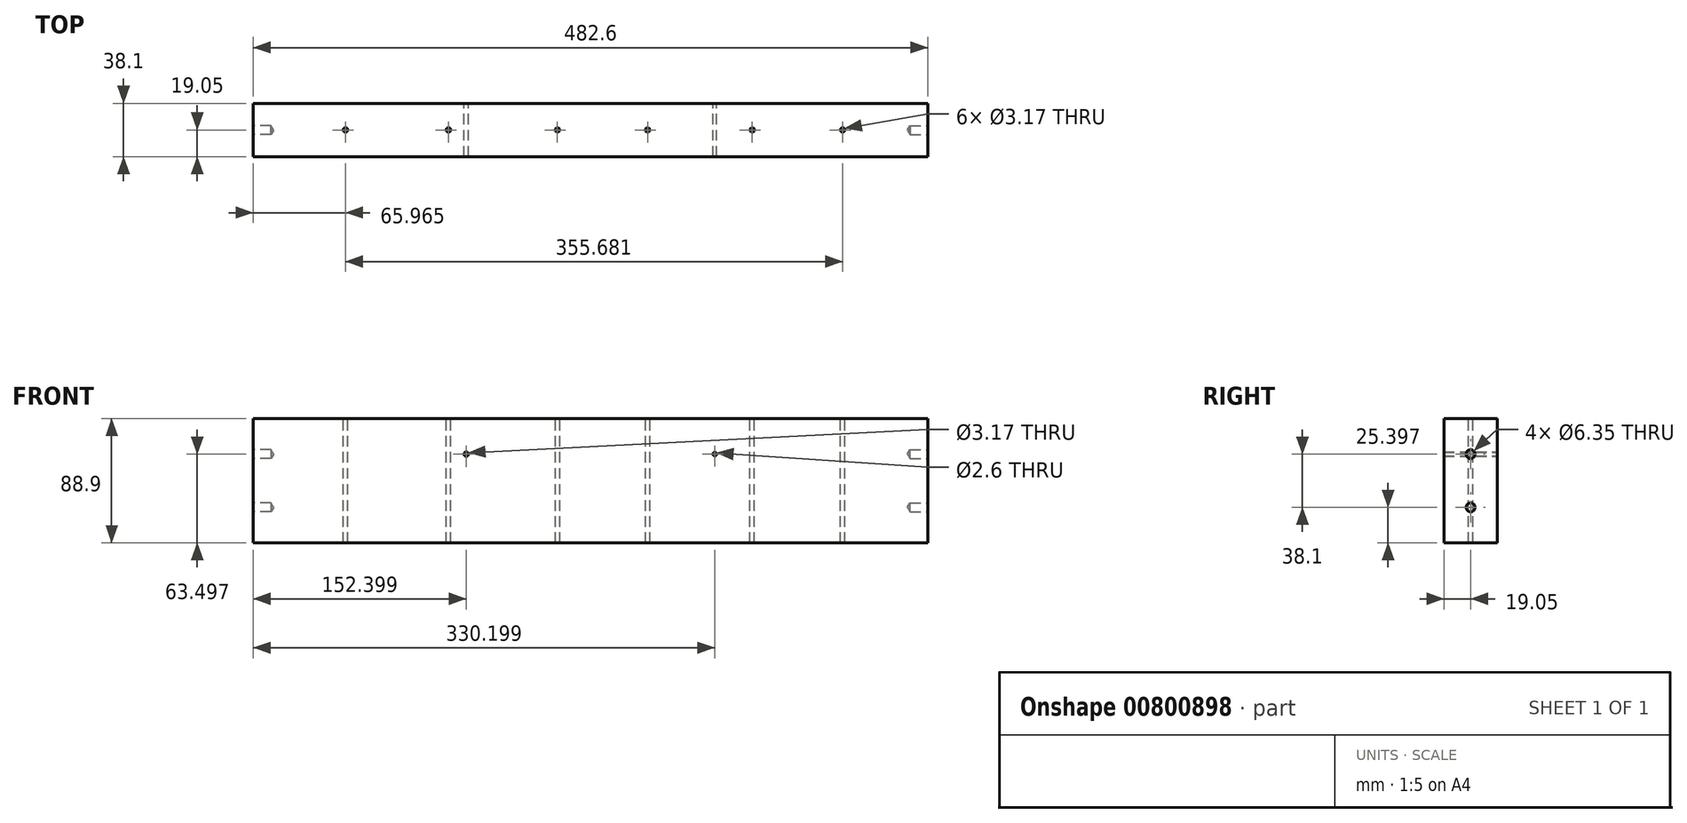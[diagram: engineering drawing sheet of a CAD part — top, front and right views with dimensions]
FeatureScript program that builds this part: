
annotation { "Feature Type Name" : "Feature", "Feature Type Description" : "" }
export const myFeature = defineFeature(function(context is Context, id is Id, definition is map)
    precondition{}
    {
        {
            var Q0;
            Q0=qCreatedBy(makeId("Front.planeOp"),FACE);
            var sketch = newSketch(context, id + "F0", { "sketchPlane" : qUnion([Q0])});
            skLineSegment(sketch, "E0.bottom", {"start": v(-145.95, -4.54) * mm, "end": v(336.65, -4.54) * mm});
            skLineSegment(sketch, "E0.top", {"start": v(-145.95, -93.44) * mm, "end": v(336.65, -93.44) * mm});
            skLineSegment(sketch, "E0.left", {"start": v(-145.95, -4.54) * mm, "end": v(-145.95, -93.44) * mm});
            skLineSegment(sketch, "E0.right", {"start": v(336.65, -4.54) * mm, "end": v(336.65, -93.44) * mm});
            skSolve(sketch);
        }
        {
            var Q0;
            Q0=makeQuery(id+"F0.imprint","IMPRINT",FACE,{"disambiguationData":[TD([[makeQuery(id+"F0.imprint","IMPRINT",EDGE,{"derivedFrom":sQuery(id+"F0.wireOp",EDGE,"E0.bottom")}),-1.0]])]});
            extrude(context, id + "F1", {"entities" : qUnion([Q0]), "depth" : 38.1 * mm, "offsetDistance" : 25.4 * mm});
        }
        {
            var Q0;
            Q0=makeQuery(id+"F1.opExtrude","SWEPT_FACE",FACE,{"disambiguationData":[OSD([sQuery(id+"F0.wireOp",EDGE,"E0.right")])]});
            var sketch = newSketch(context, id + "F2", { "sketchPlane" : qUnion([Q0])});
            skLineSegment(sketch, "E1", {"start": v(-19.05, -4.54) * mm, "end": v(-19.05, -93.44) * mm, "construction": true});
            skPoint(sketch, "E2", {"position": v(-19.05, -29.94) * mm});
            skPoint(sketch, "E3", {"position": v(-19.05, -68.04) * mm});
            skSolve(sketch);
        }
        {
            var Q0;
            Q0=sQuery(id+"F2.wireOp",VERTEX,"E2");
            var Q1;
            Q1=sQuery(id+"F2.wireOp",VERTEX,"E3");
            var Q2;
            Q2=makeQuery(id+"F1.opExtrude","SWEPT_BODY",BODY,{"disambiguationData":[OSD([sQuery(id+"F0.wireOp",EDGE,"E0.bottom"),sQuery(id+"F0.wireOp",EDGE,"E0.top"),sQuery(id+"F0.wireOp",EDGE,"E0.left"),sQuery(id+"F0.wireOp",EDGE,"E0.right")])]});
            hole(context, id + "F3", {"style" : HoleStyle.SIMPLE, "endStyle" : HoleEndStyle.BLIND, "holeDiameter" : 6.35 * mm, "majorDiameter" : 6.35 * mm, "holeDepth" : 12.7 * mm, "isTappedThrough" : true, "tappedDepth" : 12.7 * mm, "tapClearance" : 3, "locations" : qUnion([Q0, Q1]), "scope" : qUnion([Q2])});
        }
        {
            var Q0;
            Q0=makeQuery(id+"F1.opExtrude","SWEPT_FACE",FACE,{"disambiguationData":[OSD([sQuery(id+"F0.wireOp",EDGE,"E0.left")])]});
            var sketch = newSketch(context, id + "F4", { "sketchPlane" : qUnion([Q0])});
            skLineSegment(sketch, "E4", {"start": v(19.05, -4.54) * mm, "end": v(19.05, -93.44) * mm, "construction": true});
            skPoint(sketch, "E5", {"position": v(19.05, -29.94) * mm});
            skPoint(sketch, "E6", {"position": v(19.05, -68.04) * mm});
            skSolve(sketch);
        }
        {
            var Q0;
            Q0=sQuery(id+"F4.wireOp",VERTEX,"E5");
            var Q1;
            Q1=sQuery(id+"F4.wireOp",VERTEX,"E6");
            var Q2;
            Q2=makeQuery(id+"F1.opExtrude","SWEPT_BODY",BODY,{"disambiguationData":[OSD([sQuery(id+"F0.wireOp",EDGE,"E0.bottom"),sQuery(id+"F0.wireOp",EDGE,"E0.top"),sQuery(id+"F0.wireOp",EDGE,"E0.left"),sQuery(id+"F0.wireOp",EDGE,"E0.right")])]});
            hole(context, id + "F5", {"style" : HoleStyle.SIMPLE, "endStyle" : HoleEndStyle.BLIND, "holeDiameter" : 6.35 * mm, "majorDiameter" : 6.35 * mm, "holeDepth" : 12.7 * mm, "isTappedThrough" : true, "tappedDepth" : 12.7 * mm, "tapClearance" : 3, "locations" : qUnion([Q0, Q1]), "scope" : qUnion([Q2])});
        }
        {
            var Q0;
            Q0=makeQuery(id+"F1.opExtrude","CAP_FACE",FACE,{"disambiguationData":[OSD([sQuery(id+"F0.wireOp",EDGE,"E0.bottom"),sQuery(id+"F0.wireOp",EDGE,"E0.top"),sQuery(id+"F0.wireOp",EDGE,"E0.left"),sQuery(id+"F0.wireOp",EDGE,"E0.right")])],"isStart":true});
            var sketch = newSketch(context, id + "F6", { "sketchPlane" : qUnion([Q0])});
            skCircle(sketch, "E7", {"center": v(-184.25, -29.94) * mm, "radius": 1.3 * mm});
            skCircle(sketch, "E8", {"center": v(-6.45, -29.94) * mm, "radius": 1.59 * mm});
            skLineSegment(sketch, "E9", {"start": v(145.95, -29.94) * mm, "end": v(-336.65, -29.94) * mm, "construction": true});
            skSolve(sketch);
        }
        {
            var Q0;
            Q0=makeQuery(id+"F6.imprint","IMPRINT",FACE,{"disambiguationData":[TD([[makeQuery(id+"F6.imprint","IMPRINT",EDGE,{"derivedFrom":sQuery(id+"F6.wireOp",EDGE,"E7")}),1.0]])]});
            var Q1;
            Q1=makeQuery(id+"F6.imprint","IMPRINT",FACE,{"disambiguationData":[TD([[makeQuery(id+"F6.imprint","IMPRINT",EDGE,{"derivedFrom":sQuery(id+"F6.wireOp",EDGE,"E8")}),1.0]])]});
            extrude(context, id + "F7", {"entities" : qUnion([Q0, Q1]), "operationType" : NewBodyOperationType.REMOVE, "endBound" : BoundingType.THROUGH_ALL, "oppositeDirection" : true, "depth" : 25.4 * mm, "offsetDistance" : 25.4 * mm});
        }
        {
            var Q0;
            Q0=makeQuery(id+"F1.opExtrude","SWEPT_FACE",FACE,{"disambiguationData":[OSD([sQuery(id+"F0.wireOp",EDGE,"E0.bottom")])]});
            var sketch = newSketch(context, id + "F8", { "sketchPlane" : qUnion([Q0])});
            skLineSegment(sketch, "E10", {"start": v(336.65, -19.05) * mm, "end": v(-145.95, -19.05) * mm, "construction": true});
            skPoint(sketch, "E11", {"position": v(275.7, -19.05) * mm});
            skPoint(sketch, "E12", {"position": v(211.05, -19.05) * mm});
            skPoint(sketch, "E13", {"position": v(136.17, -19.05) * mm});
            skPoint(sketch, "E14", {"position": v(71.7, -19.05) * mm});
            skPoint(sketch, "E15", {"position": v(-6.34, -19.05) * mm});
            skPoint(sketch, "E16", {"position": v(-79.99, -19.05) * mm});
            skSolve(sketch);
        }
        {
            var Q0;
            Q0=sQuery(id+"F8.wireOp",VERTEX,"E11");
            var Q1;
            Q1=sQuery(id+"F8.wireOp",VERTEX,"E12");
            var Q2;
            Q2=sQuery(id+"F8.wireOp",VERTEX,"E13");
            var Q3;
            Q3=sQuery(id+"F8.wireOp",VERTEX,"E14");
            var Q4;
            Q4=sQuery(id+"F8.wireOp",VERTEX,"E15");
            var Q5;
            Q5=sQuery(id+"F8.wireOp",VERTEX,"E16");
            var Q6;
            Q6=makeQuery(id+"F1.opExtrude","SWEPT_BODY",BODY,{"disambiguationData":[OSD([sQuery(id+"F0.wireOp",EDGE,"E0.bottom"),sQuery(id+"F0.wireOp",EDGE,"E0.top"),sQuery(id+"F0.wireOp",EDGE,"E0.left"),sQuery(id+"F0.wireOp",EDGE,"E0.right")])]});
            hole(context, id + "F9", {"style" : HoleStyle.SIMPLE, "endStyle" : HoleEndStyle.THROUGH, "holeDiameter" : 3.17 * mm, "majorDiameter" : 6.35 * mm, "isTappedThrough" : true, "tappedDepth" : 12.7 * mm, "tapClearance" : 3, "locations" : qUnion([Q0, Q1, Q2, Q3, Q4, Q5]), "scope" : qUnion([Q6])});
        }
    });
